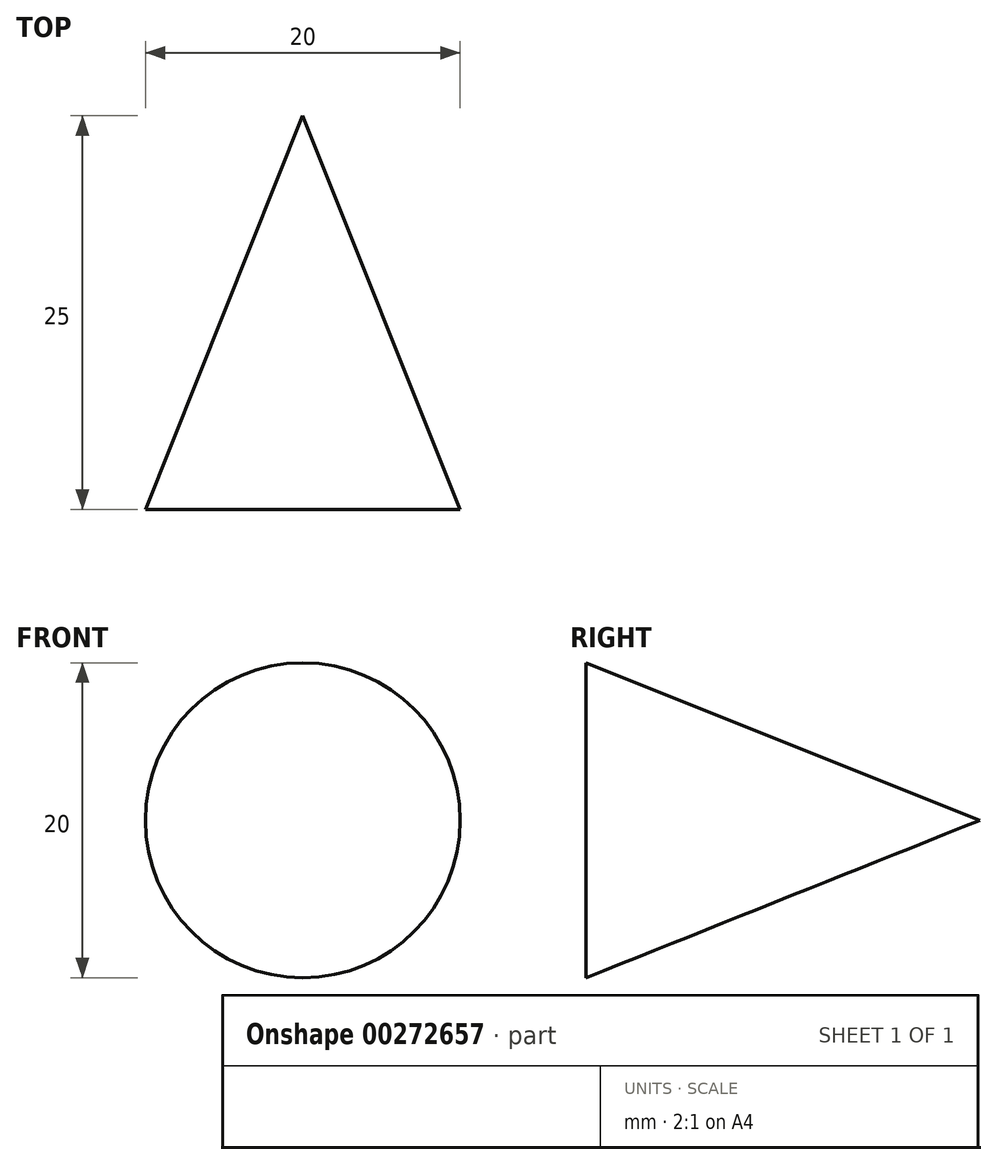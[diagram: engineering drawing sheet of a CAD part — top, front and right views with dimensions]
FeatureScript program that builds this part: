
annotation { "Feature Type Name" : "Feature", "Feature Type Description" : "" }
export const myFeature = defineFeature(function(context is Context, id is Id, definition is map)
    precondition{}
    {
        {
            var Q0;
            Q0=qCreatedBy(makeId("Front.planeOp"),FACE);
            var sketch = newSketch(context, id + "F0", { "sketchPlane" : qUnion([Q0])});
            skCircle(sketch, "E0", {"center": v(0, 0) * mm, "radius": 10 * mm});
            skSolve(sketch);
        }
        {
            var Q0;
            Q0=makeQuery(id+"F0.imprint","IMPRINT",FACE,{"disambiguationData":[TD([[makeQuery(id+"F0.imprint","IMPRINT",EDGE,{"derivedFrom":sQuery(id+"F0.wireOp",EDGE,"E0")}),1.0]])]});
            extrude(context, id + "F1", {"entities" : qUnion([Q0]), "depth" : 25 * mm, "offsetDistance" : 25 * mm});
        }
        {
            var Q0;
            Q0=makeQuery(id+"F1.opExtrude","CAP_FACE",FACE,{"disambiguationData":[OSD([sQuery(id+"F0.wireOp",EDGE,"E0")])],"isStart":true});
            var sketch = newSketch(context, id + "F2", { "sketchPlane" : qUnion([Q0])});
            skCircle(sketch, "E1", {"center": v(0, 0) * mm, "radius": 3.8 * mm});
            skSolve(sketch);
        }
        {
            var Q0;
            Q0=makeQuery(id+"F2.imprint","IMPRINT",FACE,{"disambiguationData":[TD([[makeQuery(id+"F2.imprint","IMPRINT",EDGE,{"derivedFrom":sQuery(id+"F2.wireOp",EDGE,"E1")}),-1.0]])]});
            var sketch = newSketch(context, id + "F3", { "sketchPlane" : qUnion([Q0])});
            skCircle(sketch, "E2", {"center": v(0, 0) * mm, "radius": 2.44 * mm});
            skSolve(sketch);
        }
        {
            var Q1;
            Q1=makeQuery(id+"F1.opExtrude","CAP_FACE",FACE,{"disambiguationData":[OSD([sQuery(id+"F0.wireOp",EDGE,"E0")])],"isStart":false});
            var Q2;
            Q2=sQuery(id+"F3.wireOp",VERTEX,"E2.center");
            loft(context, id + "F4", {"operationType" : NewBodyOperationType.INTERSECT, "sheetProfilesArray" : [{ "sheetProfileEntities" : qUnion([Q1]) }, { "sheetProfileEntities" : qUnion([Q2]) }]});
        }
    });
